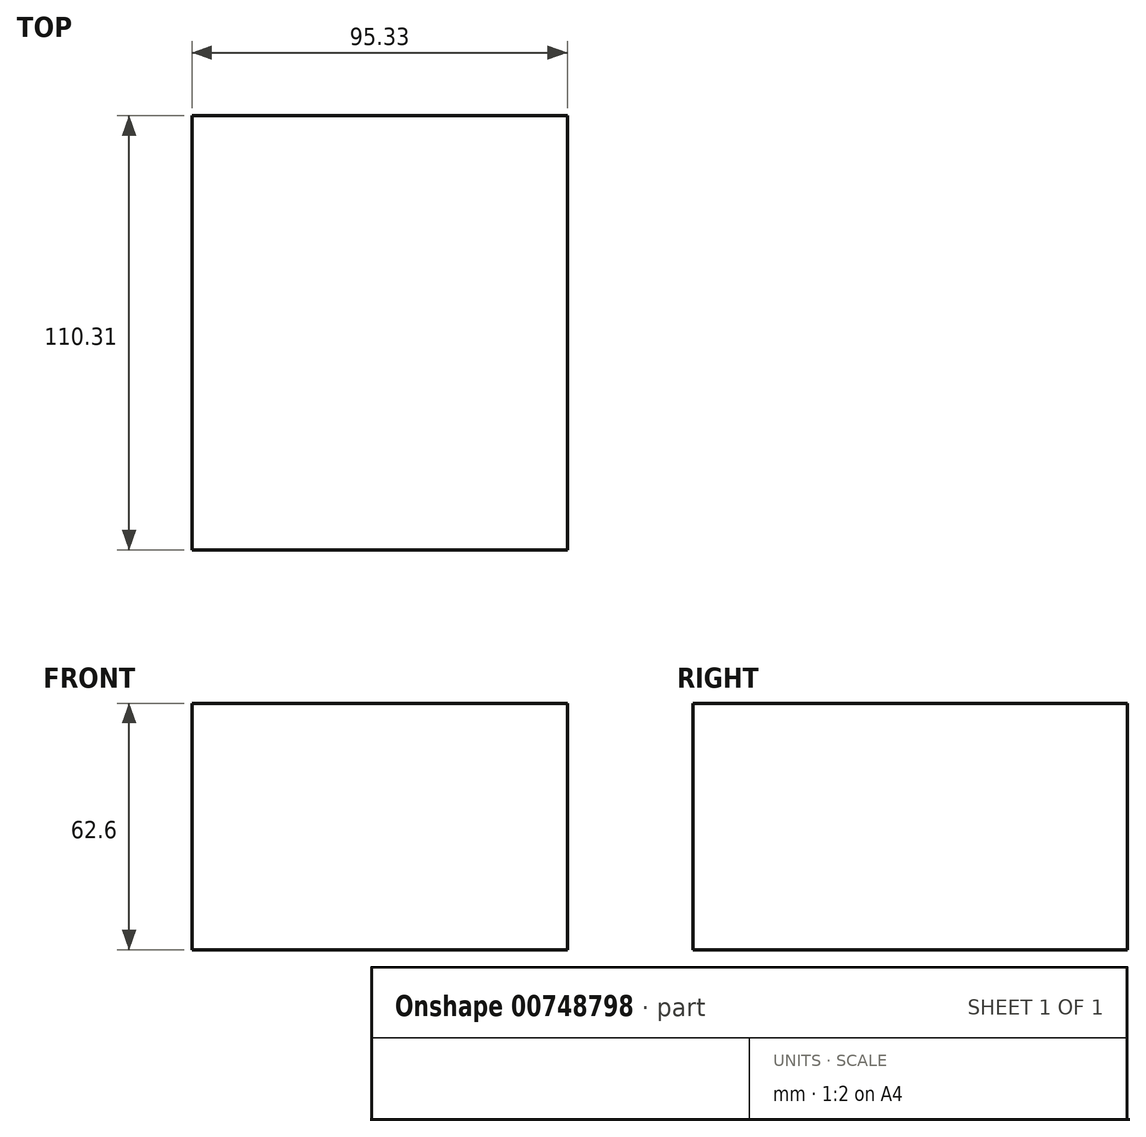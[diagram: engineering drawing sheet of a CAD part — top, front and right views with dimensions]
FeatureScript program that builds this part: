
annotation { "Feature Type Name" : "Feature", "Feature Type Description" : "" }
export const myFeature = defineFeature(function(context is Context, id is Id, definition is map)
    precondition{}
    {
        {
            var Q0;
            Q0=qCreatedBy(makeId("Front.planeOp"),FACE);
            var sketch = newSketch(context, id + "F0", { "sketchPlane" : qUnion([Q0])});
            skLineSegment(sketch, "E0.bottom", {"start": v(46.84, 0) * mm, "end": v(-48.5, 0) * mm});
            skLineSegment(sketch, "E0.top", {"start": v(46.84, -62.6) * mm, "end": v(-48.5, -62.6) * mm});
            skLineSegment(sketch, "E0.left", {"start": v(46.84, 0) * mm, "end": v(46.84, -62.6) * mm});
            skLineSegment(sketch, "E0.right", {"start": v(-48.5, 0) * mm, "end": v(-48.5, -62.6) * mm});
            skSolve(sketch);
        }
        {
            var Q0;
            Q0 = qSketchRegion(id + "F0", true);
            extrude(context, id + "F1", {"entities" : qUnion([Q0]), "oppositeDirection" : true, "depth" : 110.31 * mm, "offsetDistance" : 25 * mm});
        }
    });
